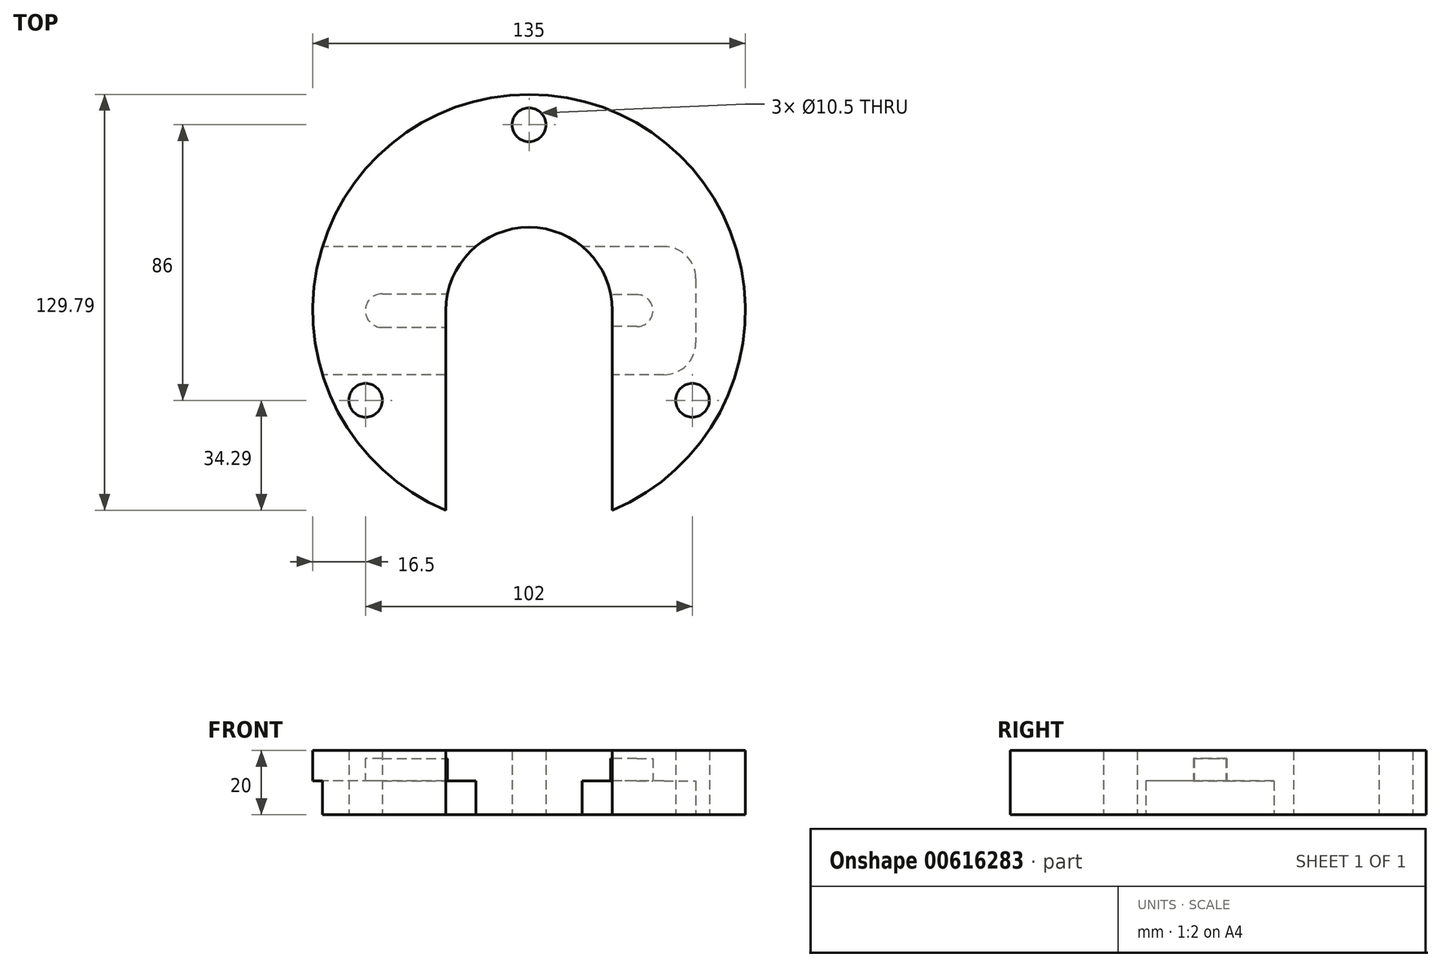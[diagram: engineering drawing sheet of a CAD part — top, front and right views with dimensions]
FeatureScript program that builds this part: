
annotation { "Feature Type Name" : "Feature", "Feature Type Description" : "" }
export const myFeature = defineFeature(function(context is Context, id is Id, definition is map)
    precondition{}
    {
        {
            var Q0;
            Q0=qCreatedBy(makeId("Top.planeOp"),FACE);
            var sketch = newSketch(context, id + "F0", { "sketchPlane" : qUnion([Q0])});
            skCircle(sketch, "E0", {"center": v(0, 0) * mm, "radius": 67.5 * mm});
            skCircle(sketch, "E1", {"center": v(0, 0) * mm, "radius": 26 * mm});
            skLineSegment(sketch, "E2", {"start": v(-26, 0) * mm, "end": v(-26, -62.3) * mm});
            skLineSegment(sketch, "E3", {"start": v(26, 0) * mm, "end": v(26, -62.3) * mm});
            skCircle(sketch, "E4", {"center": v(0, 58) * mm, "radius": 5.25 * mm});
            skCircle(sketch, "E5", {"center": v(-51, -28) * mm, "radius": 5.25 * mm});
            skCircle(sketch, "E6", {"center": v(51, -28) * mm, "radius": 5.25 * mm});
            skSolve(sketch);
        }
        {
            var Q0;
            {var subQ1=sQuery(id+"F0.wireOp",EDGE,"E1");var subQ12=sQuery(id+"F0.wireOp",EDGE,"E2");var subQ13=makeQuery(id+"F0.imprint","INTERSECT",VERTEX,{"derivedFrom":[subQ1,subQ12]});Q0=makeQuery(id+"F0.imprint","IMPRINT",FACE,{"disambiguationData":[TD([[makeQuery(id+"F0.imprint","IMPRINT",EDGE,{"disambiguationData":[TD([[subQ13,1.0]])],"derivedFrom":subQ1}),-1.0]])]});}
            var Q1;
            {var subQ6=sQuery(id+"F0.wireOp",EDGE,"E0");var subQ10=sQuery(id+"F0.wireOp",EDGE,"E2");var subQ11=makeQuery(id+"F0.imprint","INTERSECT",VERTEX,{"derivedFrom":[subQ6,subQ10]});Q1=makeQuery(id+"F0.imprint","IMPRINT",FACE,{"disambiguationData":[TD([[makeQuery(id+"F0.imprint","IMPRINT",EDGE,{"disambiguationData":[TD([[subQ11,1.0]])],"derivedFrom":subQ6}),1.0]])]});}
            extrude(context, id + "F1", {"entities" : qUnion([Q0, Q1]), "depth" : 20 * mm, "offsetDistance" : 25 * mm});
        }
        {
            var Q0;
            Q0=makeQuery(id+"F1.opExtrude","CAP_FACE",FACE,{"disambiguationData":[OSD([sQuery(id+"F0.wireOp",EDGE,"E0"),sQuery(id+"F0.wireOp",EDGE,"E1"),sQuery(id+"F0.wireOp",EDGE,"E2"),sQuery(id+"F0.wireOp",EDGE,"E3"),sQuery(id+"F0.wireOp",EDGE,"E4"),sQuery(id+"F0.wireOp",EDGE,"E5"),sQuery(id+"F0.wireOp",EDGE,"E6")])],"isStart":true});
            var sketch = newSketch(context, id + "F2", { "sketchPlane" : qUnion([Q0])});
            skLineSegment(sketch, "E7", {"start": v(52.04, -20) * mm, "end": v(-64.47, -20) * mm});
            skLineSegment(sketch, "E8", {"start": v(52.04, -20) * mm, "end": v(52.04, 20) * mm});
            skLineSegment(sketch, "E9", {"start": v(52.04, 20) * mm, "end": v(-64.47, 20) * mm});
            skSolve(sketch);
        }
        {
            var Q0;
            {var subQ5=sQuery(id+"F2.wireOp",EDGE,"E8");Q0=makeQuery(id+"F2.imprint","IMPRINT",FACE,{"disambiguationData":[TD([[makeQuery(id+"F2.imprint","IMPRINT",EDGE,{"derivedFrom":subQ5}),1.0]])]});}
            var Q1;
            {var subQ3=sQuery(id+"F2.wireOp",EDGE,"E7");var subQ5=makeQuery(id+"F1.opExtrude","CAP_EDGE",EDGE,{"disambiguationData":[OSD([sQuery(id+"F0.wireOp",EDGE,"E0")])],"isStart":true});var subQ6=makeQuery(id+"F2.imprint","INTERSECT",VERTEX,{"derivedFrom":[subQ5,subQ3]});Q1=makeQuery(id+"F2.imprint","IMPRINT",FACE,{"disambiguationData":[TD([[makeQuery(id+"F2.imprint","IMPRINT",EDGE,{"disambiguationData":[TD([[subQ6,1.0]])],"derivedFrom":subQ3}),-1.0]])]});}
            extrude(context, id + "F3", {"entities" : qUnion([Q0, Q1]), "operationType" : NewBodyOperationType.REMOVE, "oppositeDirection" : true, "depth" : 10.5 * mm, "offsetDistance" : 25 * mm});
        }
        {
            var Q0;
            Q0=makeQuery(id+"F3.boolean.opBoolean","COPY",EDGE,{"derivedFrom":makeQuery(id+"F3.opExtrude","SWEPT_EDGE",EDGE,{"disambiguationData":[OSD([sQuery(id+"F2.wireOp",EDGE,"E7"),sQuery(id+"F2.wireOp",EDGE,"E8")])]})});
            var Q1;
            Q1=makeQuery(id+"F3.boolean.opBoolean","COPY",EDGE,{"derivedFrom":makeQuery(id+"F3.opExtrude","SWEPT_EDGE",EDGE,{"disambiguationData":[OSD([sQuery(id+"F2.wireOp",EDGE,"E8"),sQuery(id+"F2.wireOp",EDGE,"E9")])]})});
            fillet(context, id + "F4", {"entities" : qUnion([Q0, Q1]), "radius" : 10 * mm, "tangentPropagation" : true, "allowEdgeOverflow" : false});
        }
        {
            var Q0;
            Q0=makeQuery(id+"F3.boolean.opBoolean","COPY",FACE,{"derivedFrom":makeQuery(id+"F3.opExtrude","CAP_FACE",FACE,{"disambiguationData":[OSD([sQuery(id+"F0.wireOp",EDGE,"E1"),sQuery(id+"F0.wireOp",EDGE,"E3"),sQuery(id+"F2.wireOp",EDGE,"E7"),sQuery(id+"F2.wireOp",EDGE,"E8"),sQuery(id+"F2.wireOp",EDGE,"E9")])],"isStart":false})});
            var sketch = newSketch(context, id + "F5", { "sketchPlane" : qUnion([Q0])});
            skCircle(sketch, "E10", {"center": v(33.63, 0) * mm, "radius": 5 * mm});
            skLineSegment(sketch, "E11", {"start": v(33.63, 5) * mm, "end": v(26, 5) * mm});
            skLineSegment(sketch, "E12", {"start": v(33.63, -5) * mm, "end": v(25.51, -5) * mm});
            skSolve(sketch);
        }
        {
            var Q0;
            {var subQ0=sQuery(id+"F5.wireOp",EDGE,"E10");var subQ1=makeQuery(id+"F5.imprint","INTERSECT",VERTEX,{"derivedFrom":[subQ0,sQuery(id+"F5.wireOp",EDGE,"E11")]});Q0=makeQuery(id+"F5.imprint","IMPRINT",FACE,{"disambiguationData":[TD([[makeQuery(id+"F5.imprint","IMPRINT",EDGE,{"disambiguationData":[TD([[subQ1,-1.0]])],"derivedFrom":subQ0}),1.0]])]});}
            var Q1;
            {var subQ7=sQuery(id+"F5.wireOp",EDGE,"E11");Q1=makeQuery(id+"F5.imprint","IMPRINT",FACE,{"disambiguationData":[TD([[makeQuery(id+"F5.imprint","IMPRINT",EDGE,{"derivedFrom":subQ7}),1.0]])]});}
            extrude(context, id + "F6", {"entities" : qUnion([Q0, Q1]), "operationType" : NewBodyOperationType.REMOVE, "oppositeDirection" : true, "depth" : 7 * mm, "offsetDistance" : 25 * mm});
        }
        {
            var Q0;
            Q0=makeQuery(id+"F3.boolean.opBoolean","COPY",FACE,{"derivedFrom":makeQuery(id+"F3.opExtrude","CAP_FACE",FACE,{"disambiguationData":[OSD([sQuery(id+"F0.wireOp",EDGE,"E0"),sQuery(id+"F0.wireOp",EDGE,"E1"),sQuery(id+"F0.wireOp",EDGE,"E2"),sQuery(id+"F2.wireOp",EDGE,"E7"),sQuery(id+"F2.wireOp",EDGE,"E9")])],"isStart":false})});
            var sketch = newSketch(context, id + "F7", { "sketchPlane" : qUnion([Q0])});
            skCircle(sketch, "E13", {"center": v(-45.82, 0) * mm, "radius": 5.25 * mm});
            skLineSegment(sketch, "E14", {"start": v(-45.82, 5.25) * mm, "end": v(-26, 5.25) * mm});
            skLineSegment(sketch, "E15", {"start": v(-45.82, -5.25) * mm, "end": v(-25.46, -5.25) * mm});
            skSolve(sketch);
        }
        {
            var Q0;
            {var subQ0=sQuery(id+"F7.wireOp",EDGE,"E13");var subQ1=makeQuery(id+"F7.imprint","INTERSECT",VERTEX,{"derivedFrom":[subQ0,sQuery(id+"F7.wireOp",EDGE,"E14")]});Q0=makeQuery(id+"F7.imprint","IMPRINT",FACE,{"disambiguationData":[TD([[makeQuery(id+"F7.imprint","IMPRINT",EDGE,{"disambiguationData":[TD([[subQ1,-1.0]])],"derivedFrom":subQ0}),1.0]])]});}
            var Q1;
            {var subQ7=sQuery(id+"F7.wireOp",EDGE,"E14");Q1=makeQuery(id+"F7.imprint","IMPRINT",FACE,{"disambiguationData":[TD([[makeQuery(id+"F7.imprint","IMPRINT",EDGE,{"derivedFrom":subQ7}),-1.0]])]});}
            extrude(context, id + "F8", {"entities" : qUnion([Q0, Q1]), "operationType" : NewBodyOperationType.REMOVE, "oppositeDirection" : true, "depth" : 7 * mm, "offsetDistance" : 25 * mm});
        }
    });
